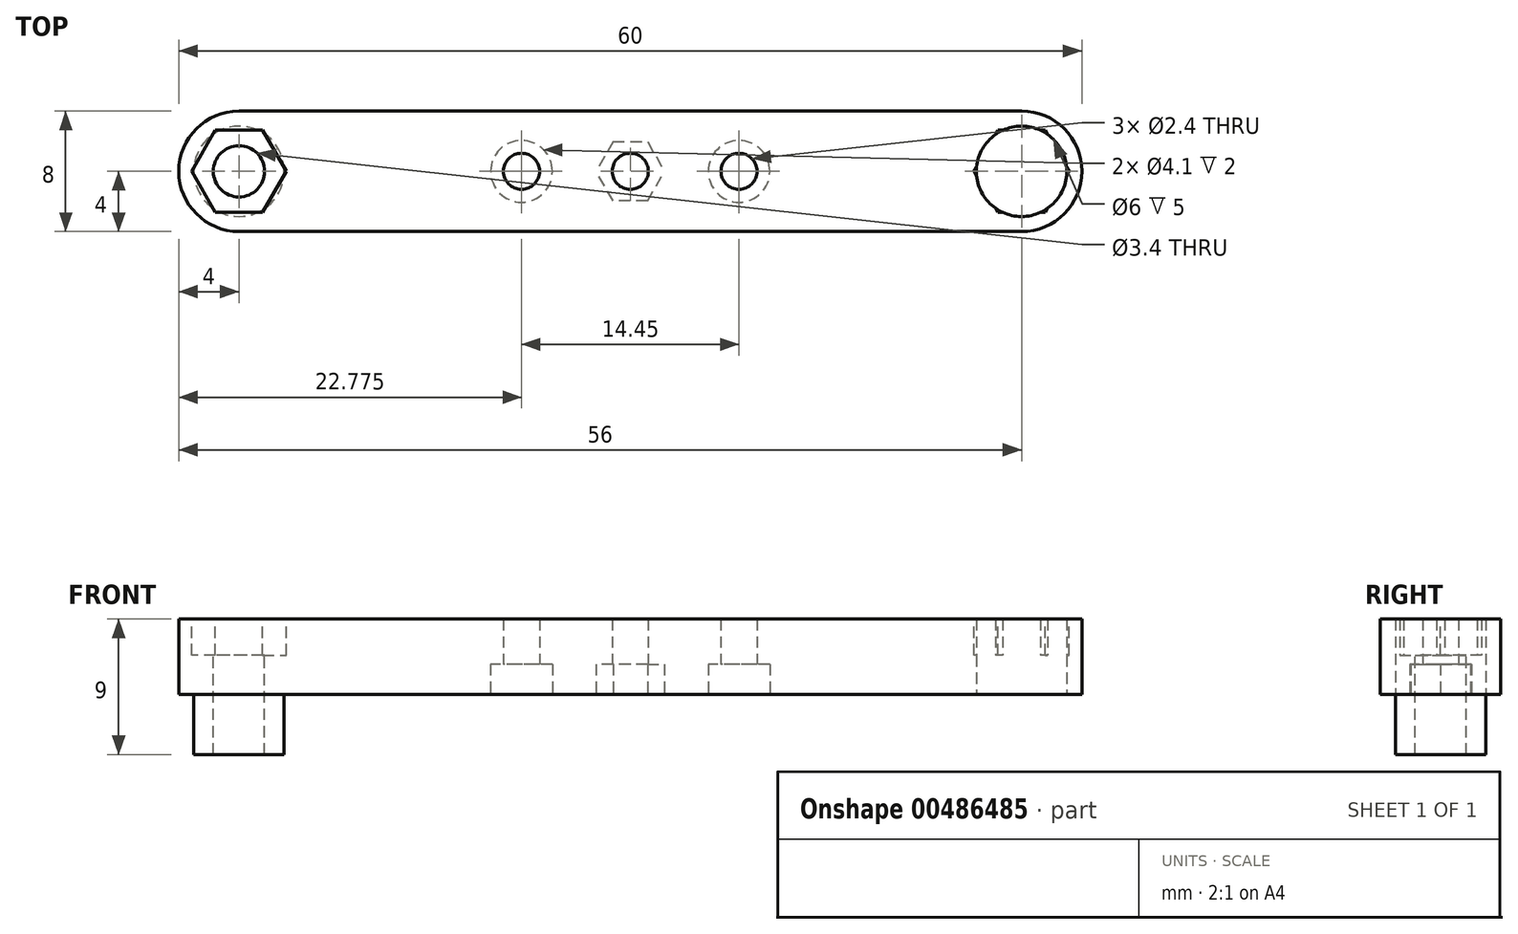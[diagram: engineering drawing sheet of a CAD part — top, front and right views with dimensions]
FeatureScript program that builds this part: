
annotation { "Feature Type Name" : "Feature", "Feature Type Description" : "" }
export const myFeature = defineFeature(function(context is Context, id is Id, definition is map)
    precondition{}
    {
        {
            var Q0;
            Q0=qCreatedBy(makeId("Top.planeOp"),FACE);
            var sketch = newSketch(context, id + "F0", { "sketchPlane" : qUnion([Q0])});
            skCircle(sketch, "E0", {"center": v(-26, 38) * mm, "radius": 1.7 * mm});
            skCircle(sketch, "E1.MirrorC", {"center": v(26, 38) * mm, "radius": 1.7 * mm});
            skCircle(sketch, "E2.MirrorC", {"center": v(-26, -38) * mm, "radius": 1.7 * mm});
            skCircle(sketch, "E3.MirrorC", {"center": v(26, -38) * mm, "radius": 1.7 * mm});
            skSolve(sketch);
        }
        {
            var Q0;
            Q0=qCreatedBy(makeId("Top.planeOp"),FACE);
            var sketch = newSketch(context, id + "F1", { "sketchPlane" : qUnion([Q0])});
            skCircle(sketch, "E4", {"center": v(-26, 38) * mm, "radius": 3 * mm});
            skCircle(sketch, "E5", {"center": v(-26, 38) * mm, "radius": 1.7 * mm});
            skCircle(sketch, "E6.MirrorC", {"center": v(26, 38) * mm, "radius": 1.7 * mm});
            skCircle(sketch, "E7.MirrorC", {"center": v(26, 38) * mm, "radius": 3 * mm});
            skLineSegment(sketch, "E8.bottom", {"start": v(-30, 42) * mm, "end": v(30, 42) * mm});
            skLineSegment(sketch, "E8.top", {"start": v(-30, 34) * mm, "end": v(30, 34) * mm});
            skLineSegment(sketch, "E8.left", {"start": v(-30, 42) * mm, "end": v(-30, 34) * mm});
            skLineSegment(sketch, "E8.right", {"start": v(30, 42) * mm, "end": v(30, 34) * mm});
            skSolve(sketch);
        }
        {
            var Q0;
            Q0=makeQuery(id+"F1.imprint","IMPRINT",FACE,{"disambiguationData":[TD([[makeQuery(id+"F1.imprint","IMPRINT",EDGE,{"derivedFrom":sQuery(id+"F1.wireOp",EDGE,"E4")}),-1.0]])]});
            var sketch = newSketch(context, id + "F2", { "sketchPlane" : qUnion([Q0])});
            skLineSegment(sketch, "E9", {"start": v(0, 38) * mm, "end": v(1.44, 35.5) * mm, "construction": true});
            skLineSegment(sketch, "E10", {"start": v(0, 38) * mm, "end": v(0, 36.02) * mm, "construction": true});
            skLineSegment(sketch, "E11", {"start": v(0, 36.02) * mm, "end": v(-1.14, 36.02) * mm});
            skLineSegment(sketch, "E12", {"start": v(-1.14, 36.02) * mm, "end": v(-2.28, 38) * mm});
            skLineSegment(sketch, "E13", {"start": v(-2.28, 38) * mm, "end": v(0, 38) * mm, "construction": true});
            skLineSegment(sketch, "E14.MirrorCS", {"start": v(-1.14, 39.97) * mm, "end": v(-2.28, 38) * mm});
            skLineSegment(sketch, "E15.MirrorCS", {"start": v(0, 39.97) * mm, "end": v(-1.14, 39.97) * mm});
            skLineSegment(sketch, "E16.MirrorCS", {"start": v(0, 36.02) * mm, "end": v(1.14, 36.02) * mm});
            skLineSegment(sketch, "E17.MirrorCS", {"start": v(1.14, 36.02) * mm, "end": v(2.28, 38) * mm});
            skLineSegment(sketch, "E18.MirrorCS", {"start": v(1.14, 39.97) * mm, "end": v(2.28, 38) * mm});
            skLineSegment(sketch, "E19.MirrorCS", {"start": v(0, 39.97) * mm, "end": v(1.14, 39.97) * mm});
            skSolve(sketch);
        }
        {
            var Q0;
            Q0=makeQuery(id+"F2.imprint","IMPRINT",FACE,{"disambiguationData":[TD([[makeQuery(id+"F2.imprint","IMPRINT",EDGE,{"derivedFrom":sQuery(id+"F2.wireOp",EDGE,"E11")}),1.0]])]});
            var sketch = newSketch(context, id + "F3", { "sketchPlane" : qUnion([Q0])});
            skCircle(sketch, "E20", {"center": v(-7.22, 38) * mm, "radius": 2.05 * mm});
            skCircle(sketch, "E21.MirrorC", {"center": v(7.22, 38) * mm, "radius": 2.05 * mm});
            skSolve(sketch);
        }
        {
            var Q0;
            Q0=makeQuery(id+"F1.imprint","IMPRINT",FACE,{"disambiguationData":[TD([[makeQuery(id+"F1.imprint","IMPRINT",EDGE,{"derivedFrom":sQuery(id+"F1.wireOp",EDGE,"E4")}),-1.0]])]});
            var sketch = newSketch(context, id + "F4", { "sketchPlane" : qUnion([Q0])});
            skCircle(sketch, "E22", {"center": v(-7.22, 38) * mm, "radius": 1.2 * mm});
            skCircle(sketch, "E23", {"center": v(0, 38) * mm, "radius": 1.2 * mm});
            skCircle(sketch, "E24.MirrorC", {"center": v(7.22, 38) * mm, "radius": 1.2 * mm});
            skSolve(sketch);
        }
        {
            var Q0;
            Q0=makeQuery(id+"F2.imprint","IMPRINT",FACE,{"disambiguationData":[TD([[makeQuery(id+"F2.imprint","IMPRINT",EDGE,{"derivedFrom":sQuery(id+"F2.wireOp",EDGE,"E11")}),1.0]])]});
            var Q1;
            Q1=makeQuery(id+"F2.imprint","IMPRINT",FACE,{"disambiguationData":[TD([[makeQuery(id+"F2.imprint","IMPRINT",EDGE,{"derivedFrom":sQuery(id+"F2.wireOp",EDGE,"E11")}),-1.0]])]});
            var Q2;
            Q2=makeQuery(id+"F2.imprint","IMPRINT",FACE,{"disambiguationData":[TD([[makeQuery(id+"F2.imprint","IMPRINT",EDGE,{"derivedFrom":makeQuery(id+"F1.imprint","IMPRINT",EDGE,{"derivedFrom":sQuery(id+"F1.wireOp",EDGE,"E4")})}),1.0]])]});
            var Q3;
            Q3=makeQuery(id+"F2.imprint","IMPRINT",FACE,{"disambiguationData":[TD([[makeQuery(id+"F2.imprint","IMPRINT",EDGE,{"derivedFrom":makeQuery(id+"F1.imprint","IMPRINT",EDGE,{"derivedFrom":sQuery(id+"F1.wireOp",EDGE,"E7.MirrorC")})}),-1.0]])]});
            extrude(context, id + "F5", {"entities" : qUnion([Q0, Q1, Q2, Q3]), "depth" : 5 * mm, "offsetDistance" : 25 * mm});
        }
        {
            var Q0;
            Q0=makeQuery(id+"F1.imprint","IMPRINT",FACE,{"disambiguationData":[TD([[makeQuery(id+"F1.imprint","IMPRINT",EDGE,{"derivedFrom":sQuery(id+"F1.wireOp",EDGE,"E4")}),1.0]])]});
            var Q1;
            Q1=makeQuery(id+"F1.imprint","IMPRINT",FACE,{"disambiguationData":[TD([[makeQuery(id+"F1.imprint","IMPRINT",EDGE,{"derivedFrom":sQuery(id+"F1.wireOp",EDGE,"E6.MirrorC")}),1.0]])]});
            extrude(context, id + "F6", {"entities" : qUnion([Q0, Q1]), "operationType" : NewBodyOperationType.ADD, "oppositeDirection" : true, "depth" : 4 * mm, "offsetDistance" : 25 * mm});
        }
        {
            var Q0;
            Q0 = qSketchRegion(id + "F0", true);
            extrude(context, id + "F7", {"entities" : qUnion([Q0]), "operationType" : NewBodyOperationType.REMOVE, "oppositeDirection" : true, "depth" : 25 * mm, "offsetDistance" : 25 * mm, "symmetric" : true});
        }
        {
            var Q0;
            Q0 = qSketchRegion(id + "F3", true);
            var Q1;
            Q1=sQuery(id+"F3.wireOp",EDGE,"E20");
            var Q2;
            Q2=sQuery(id+"F3.wireOp",EDGE,"E21.MirrorC");
            extrude(context, id + "F8", {"entities" : qUnion([Q0]), "operationType" : NewBodyOperationType.REMOVE, "surfaceEntities" : qUnion([Q1, Q2]), "depth" : 2 * mm, "offsetDistance" : 25 * mm});
        }
        {
            var Q0;
            Q0 = qSketchRegion(id + "F2", true);
            extrude(context, id + "F9", {"entities" : qUnion([Q0]), "operationType" : NewBodyOperationType.REMOVE, "depth" : 2 * mm, "offsetDistance" : 25 * mm});
        }
        {
            var Q0;
            Q0=makeQuery(id+"F5.opExtrude","CAP_FACE",FACE,{"disambiguationData":[OSD([sQuery(id+"F1.wireOp",EDGE,"E8.bottom"),sQuery(id+"F1.wireOp",EDGE,"E8.top"),sQuery(id+"F1.wireOp",EDGE,"E8.left"),sQuery(id+"F1.wireOp",EDGE,"E8.right")])],"isStart":false});
            var sketch = newSketch(context, id + "F10", { "sketchPlane" : qUnion([Q0])});
            skLineSegment(sketch, "E25", {"start": v(-26, 38) * mm, "end": v(-26, 35.27) * mm, "construction": true});
            skLineSegment(sketch, "E26", {"start": v(-26, 35.27) * mm, "end": v(-26, 38) * mm, "construction": true});
            skLineSegment(sketch, "E27", {"start": v(-26, 38) * mm, "end": v(-25.14, 36.51) * mm, "construction": true});
            skLineSegment(sketch, "E28", {"start": v(-26, 35.27) * mm, "end": v(-27.57, 35.27) * mm});
            skLineSegment(sketch, "E29", {"start": v(-27.57, 35.27) * mm, "end": v(-29.15, 38) * mm});
            skLineSegment(sketch, "E30.MirrorCS", {"start": v(-24.43, 35.27) * mm, "end": v(-22.85, 38) * mm});
            skLineSegment(sketch, "E31.MirrorCS", {"start": v(-26, 35.27) * mm, "end": v(-24.43, 35.27) * mm});
            skLineSegment(sketch, "E32", {"start": v(-26, 38) * mm, "end": v(-29.15, 38) * mm, "construction": true});
            skLineSegment(sketch, "E33.MirrorCS", {"start": v(-27.57, 40.72) * mm, "end": v(-29.15, 38) * mm});
            skLineSegment(sketch, "E34.MirrorCS", {"start": v(-26, 40.72) * mm, "end": v(-27.57, 40.72) * mm});
            skLineSegment(sketch, "E35.MirrorCS", {"start": v(-26, 40.72) * mm, "end": v(-24.43, 40.72) * mm});
            skLineSegment(sketch, "E36.MirrorCS", {"start": v(-24.43, 40.72) * mm, "end": v(-22.85, 38) * mm});
            skLineSegment(sketch, "E37.MirrorCS", {"start": v(24.43, 35.27) * mm, "end": v(22.85, 38) * mm});
            skLineSegment(sketch, "E38.MirrorCS", {"start": v(24.43, 40.72) * mm, "end": v(22.85, 38) * mm});
            skLineSegment(sketch, "E39.MirrorCS", {"start": v(26, 40.72) * mm, "end": v(24.43, 40.72) * mm});
            skLineSegment(sketch, "E40.MirrorCS", {"start": v(26, 40.72) * mm, "end": v(27.57, 40.72) * mm});
            skLineSegment(sketch, "E41.MirrorCS", {"start": v(27.57, 40.72) * mm, "end": v(29.15, 38) * mm});
            skLineSegment(sketch, "E42.MirrorCS", {"start": v(27.57, 35.27) * mm, "end": v(29.15, 38) * mm});
            skLineSegment(sketch, "E43.MirrorCS", {"start": v(26, 35.27) * mm, "end": v(27.57, 35.27) * mm});
            skLineSegment(sketch, "E44.MirrorCS", {"start": v(26, 35.27) * mm, "end": v(24.43, 35.27) * mm});
            skSolve(sketch);
        }
        {
            var Q0;
            Q0 = qSketchRegion(id + "F10", true);
            extrude(context, id + "F11", {"entities" : qUnion([Q0]), "operationType" : NewBodyOperationType.REMOVE, "oppositeDirection" : true, "depth" : 2.4 * mm, "offsetDistance" : 25 * mm});
        }
        {
            var Q0;
            Q0=makeQuery(id+"F5.opExtrude","SWEPT_EDGE",EDGE,{"disambiguationData":[OSD([sQuery(id+"F1.wireOp",EDGE,"E8.bottom"),sQuery(id+"F1.wireOp",EDGE,"E8.left")])]});
            var Q1;
            Q1=makeQuery(id+"F5.opExtrude","SWEPT_EDGE",EDGE,{"disambiguationData":[OSD([sQuery(id+"F1.wireOp",EDGE,"E8.top"),sQuery(id+"F1.wireOp",EDGE,"E8.left")])]});
            var Q2;
            Q2=makeQuery(id+"F5.opExtrude","SWEPT_EDGE",EDGE,{"disambiguationData":[OSD([sQuery(id+"F1.wireOp",EDGE,"E8.bottom"),sQuery(id+"F1.wireOp",EDGE,"E8.right")])]});
            var Q3;
            Q3=makeQuery(id+"F5.opExtrude","SWEPT_EDGE",EDGE,{"disambiguationData":[OSD([sQuery(id+"F1.wireOp",EDGE,"E8.top"),sQuery(id+"F1.wireOp",EDGE,"E8.right")])]});
            fillet(context, id + "F12", {"entities" : qUnion([Q0, Q1, Q2, Q3]), "radius" : 4 * mm, "tangentPropagation" : true, "allowEdgeOverflow" : false});
        }
        {
            var Q0;
            Q0 = qSketchRegion(id + "F4", true);
            extrude(context, id + "F13", {"entities" : qUnion([Q0]), "operationType" : NewBodyOperationType.REMOVE, "endBound" : BoundingType.THROUGH_ALL, "depth" : 25 * mm, "offsetDistance" : 25 * mm});
        }
    });
